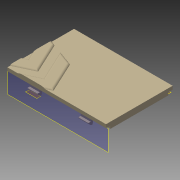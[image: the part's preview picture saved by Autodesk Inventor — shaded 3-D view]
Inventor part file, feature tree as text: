
AUTODESK INVENTOR PART (.ipt)
format: ipt  version: 2014 (Build 180170000, 170)  size: 257,024 bytes
history: native  units: mm
features: reference x26, sketch x8, other x7, extrude x7, mirror x2, chamfer x1, fillet x1
ambient origin geometry x8: Origin, YZ Plane, XZ Plane, XY Plane, X Axis, Y Axis, Z Axis, Center Point
bodies: Volumenkörper1 (feature_tree)
feature tree (52):
  other  "Deckel"
  sketch  "SkizzeStecker"  dims[d7=0.05mm d8=0.05mm]
  other  "EbeneStecker"
  extrude  "Stecker"  Depth=0.05mm
  sketch  "SkizzeLippe"  dims[d9=1.5mm d10=0.0mm d11=0.05mm]
  other  "LippeEbene"
  extrude  "Lippe"  Depth=1.5mm TaperAngle=0.0deg
  sketch  "SkizzeSchnapperarm"  dims[d12=1.5mm]
  other  "EbeneSchnapper"
  extrude  "Schnapperarm"  Depth=0.05mm
  sketch  "SkizzeSchnapper"  dims[d13=0.05mm d14=1.5mm d15=0.0mm]
  other  "EbeneSchnapperTiefe2"
  extrude  "Schnapper"  Depth=0.05mm
  chamfer  "FaseSchnapper"  Distance=1.5mm
  other  "FlächenverjüngungSchnapper"
  mirror  "SpiegelnSchnapper1"
  mirror  "SpiegelnSchnapper2"
  sketch  "Skizze6"  dims[d0=1.5mm d1=0.0mm d2=0.05mm]
  extrude  "USB"  Depth=1.5mm TaperAngle=0.0deg
  extrude  "Logo"  Depth=10.0mm
  fillet  "RundungLogo"  Radius=0.05mm
  other  "EbeneStütze"
  extrude  "Extrusion9"  Depth=2.0mm TaperAngle=0.0deg
  sketch  "SkizzeDeckel"  dims[d16=0.05mm d17=1.5mm d18=0.0mm]
  reference  "Referenz1"
  reference  "Referenz2"
  reference  "Referenz3"
  reference  "Referenz4"
  reference  "Referenz5"
  reference  "Referenz6"
  reference  "Referenz7"
  reference  "Referenz8"
  reference  "Referenz9"
  reference  "Referenz10"
  reference  "Referenz11"
  reference  "Referenz12"
  reference  "Referenz13"
  reference  "Referenz14"
  reference  "Referenz15"
  reference  "Referenz16"
  reference  "Referenz17"
  reference  "Referenz18"
  reference  "Referenz19"
  reference  "Referenz20"
  reference  "Referenz21"
  reference  "Referenz22"
  sketch  "Skizze8"  dims[d4=0.05mm d5=1.5mm d6=0.0mm]
  sketch  "SkizzeStüze"  dims[d19=1.2mm d20=1.1mm d21=45.0deg d22=2.094395mm d23=0.05mm d24=2.0mm d25=0.0mm d28=11.34464mm d32=11.34464mm d34=4.0mm d37=5.0mm d38=15.0mm d39=12.0mm d40=5.0mm d41=6.0mm d42=12.0mm d43=5.0mm d44=15.0mm d45=5.0mm d46=12.0mm d48=3.0mm d49=3.0mm d50=0.5mm d51=0.0mm d52=1.0mm d53=1.5mm d54=3.0mm d55=2.0mm d56=10.0mm d57=0.0mm]
  reference  "Referenz23"
  reference  "Referenz24"
  reference  "Referenz25"
  reference  "Referenz26"
